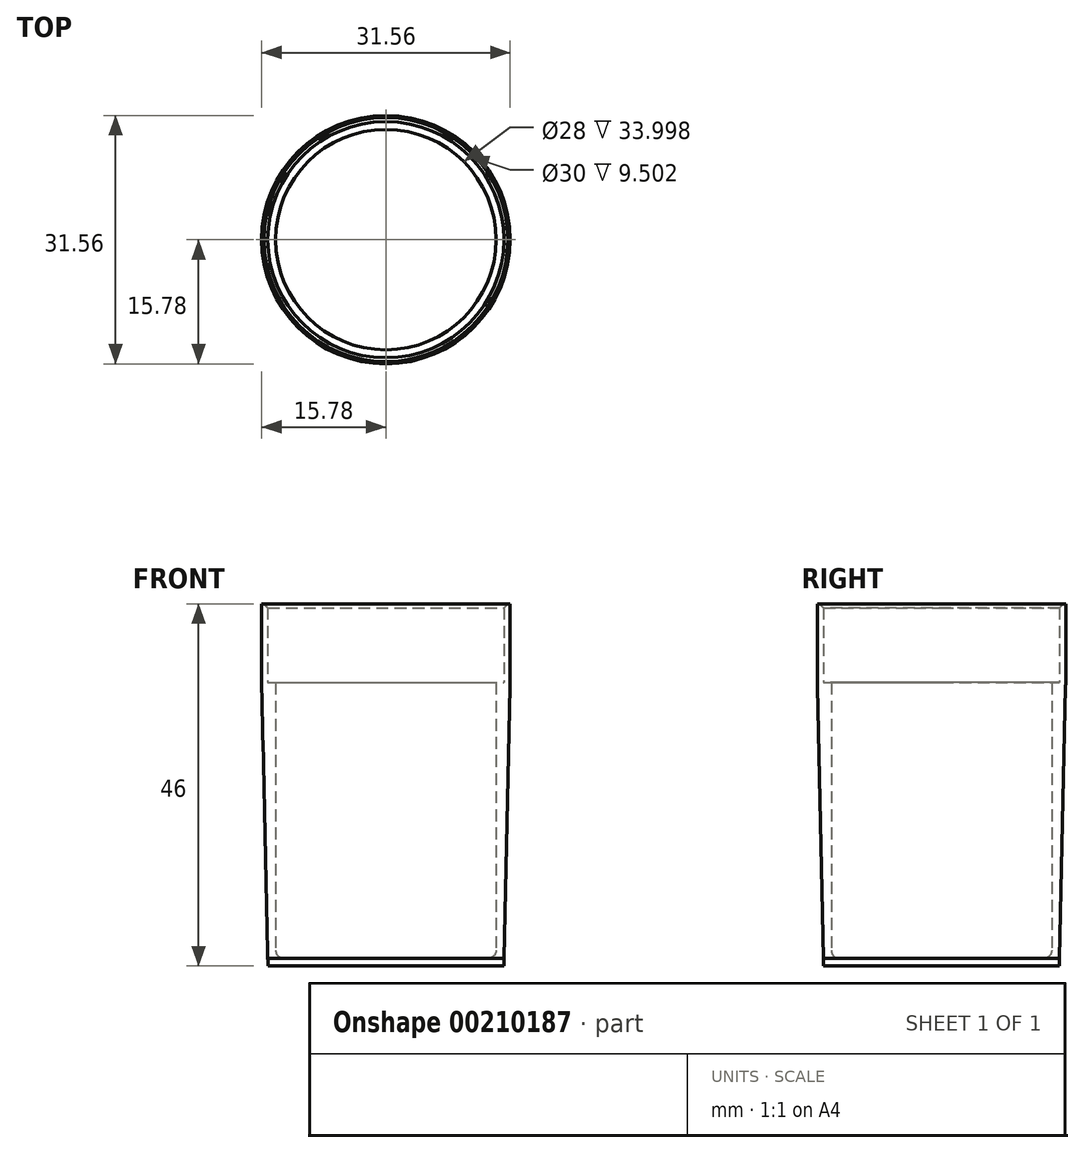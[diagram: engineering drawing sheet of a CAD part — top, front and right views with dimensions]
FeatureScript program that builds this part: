
annotation { "Feature Type Name" : "Feature", "Feature Type Description" : "" }
export const myFeature = defineFeature(function(context is Context, id is Id, definition is map)
    precondition{}
    {
        {
            var Q0;
            Q0=qCreatedBy(makeId("Front.planeOp"),FACE);
            var sketch = newSketch(context, id + "F0", { "sketchPlane" : qUnion([Q0]), "disableImprinting" : false});
            skLineSegment(sketch, "E0", {"start": v(0, 0) * mm, "end": v(0, 70.58) * mm});
            skLineSegment(sketch, "E1", {"start": v(0, 0) * mm, "end": v(-13, 0) * mm});
            skLineSegment(sketch, "E2.0", {"start": v(-14, 1) * mm, "end": v(-14, 35) * mm});
            skLineSegment(sketch, "E3.0", {"start": v(-14, 45) * mm, "end": v(-15, 45) * mm});
            skLineSegment(sketch, "E4.0", {"start": v(0, -1) * mm, "end": v(-14.98, -1) * mm});
            skLineSegment(sketch, "E5.0", {"start": v(-15, 35) * mm, "end": v(-15, 45) * mm});
            skArc(sketch, "E6.filletArc", {"start": v(-15, 0) * mm, "mid": v(-15, -0.02) * mm, "end": v(-15, -0.04) * mm});
            skArc(sketch, "E7.filletArc", {"start": v(-14, 1) * mm, "mid": v(-13.7, 0.3) * mm, "end": v(-13, 0) * mm});
            skLineSegment(sketch, "E8", {"start": v(-15.78, 35) * mm, "end": v(-15.8, 35) * mm});
            skLineSegment(sketch, "E9", {"start": v(-14.98, -1) * mm, "end": v(-15.78, 35) * mm});
            skLineSegment(sketch, "E10", {"start": v(0, -1) * mm, "end": v(0, 0) * mm});
            skLineSegment(sketch, "E11", {"start": v(-15, 45) * mm, "end": v(-15.78, 45) * mm});
            skLineSegment(sketch, "E12", {"start": v(-15, 35) * mm, "end": v(-14, 35) * mm});
            skLineSegment(sketch, "E13", {"start": v(-15.78, 35) * mm, "end": v(-15.78, 45) * mm});
            skSolve(sketch);
        }
        {
            var Q0;
            Q0=qSketchRegion(id+"F0",true);
            var Q1;
            Q1=sQuery(id+"F0.wireOp",EDGE,"E0");
            revolve(context, id + "F1", {"entities" : qUnion([Q0]), "axis" : qUnion([Q1]), "revolveType" : RevolveType.FULL});
        }
        {
            var Q0;
            Q0=makeQuery(id+"F1.opRevolve","SWEPT_EDGE",EDGE,{"disambiguationData":[OSD([sQuery(id+"F0.wireOp",EDGE,"E9"),sQuery(id+"F0.wireOp",EDGE,"E13")])]});
            fillet(context, id + "F2", {"entities" : qUnion([Q0]), "radius" : 50 * mm, "tangentPropagation" : true, "allowEdgeOverflow" : false});
        }
        {
            var Q0;
            Q0=makeQuery(id+"F1.opRevolve","SWEPT_EDGE",EDGE,{"disambiguationData":[OSD([sQuery(id+"F0.wireOp",EDGE,"E5.0"),sQuery(id+"F0.wireOp",EDGE,"E11")])]});
            chamfer(context, id + "F3", {"entities" : qUnion([Q0]), "width" : 0.5 * mm, "tangentPropagation" : true});
        }
    });
